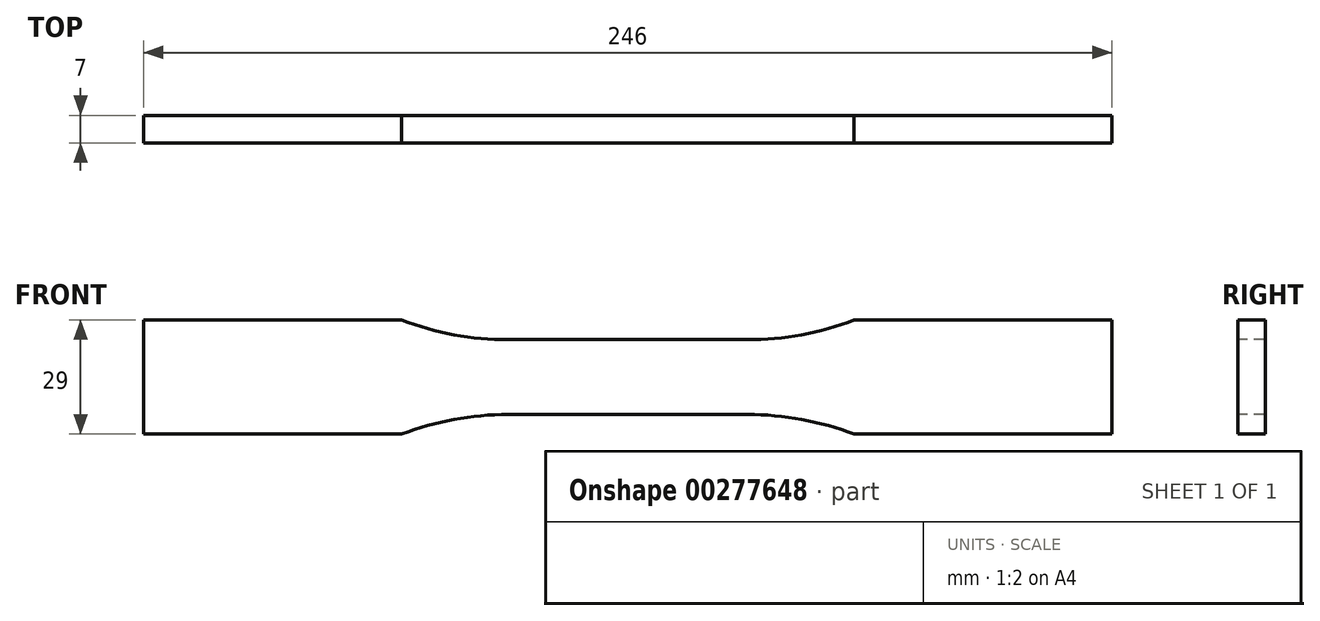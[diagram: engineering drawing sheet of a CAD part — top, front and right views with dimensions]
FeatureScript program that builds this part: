
annotation { "Feature Type Name" : "Feature", "Feature Type Description" : "" }
export const myFeature = defineFeature(function(context is Context, id is Id, definition is map)
    precondition{}
    {
        {
            var Q0;
            Q0=qCreatedBy(makeId("Front.planeOp"),FACE);
            var sketch = newSketch(context, id + "F0", { "sketchPlane" : qUnion([Q0])});
            skLineSegment(sketch, "E0", {"start": v(0, 9.5) * mm, "end": v(30.39, 9.5) * mm});
            skArc(sketch, "E1", {"start": v(30.39, 9.5) * mm, "mid": v(44.17, 10.76) * mm, "end": v(57.5, 14.5) * mm});
            skLineSegment(sketch, "E2", {"start": v(57.5, 14.5) * mm, "end": v(123, 14.5) * mm});
            skLineSegment(sketch, "E3.MirrorCS", {"start": v(57.5, -14.5) * mm, "end": v(123, -14.5) * mm});
            skLineSegment(sketch, "E4.MirrorCS", {"start": v(0, -9.5) * mm, "end": v(30.39, -9.5) * mm});
            skArc(sketch, "E5.MirrorCS", {"start": v(30.39, -9.5) * mm, "mid": v(44.17, -10.76) * mm, "end": v(57.5, -14.5) * mm});
            skArc(sketch, "E6.MirrorCS", {"start": v(-30.39, -9.5) * mm, "mid": v(-44.17, -10.76) * mm, "end": v(-57.5, -14.5) * mm});
            skLineSegment(sketch, "E7.MirrorCS", {"start": v(0, 9.5) * mm, "end": v(-30.39, 9.5) * mm});
            skArc(sketch, "E8.MirrorCS", {"start": v(-30.39, 9.5) * mm, "mid": v(-44.17, 10.76) * mm, "end": v(-57.5, 14.5) * mm});
            skLineSegment(sketch, "E9.MirrorCS", {"start": v(-57.5, -14.5) * mm, "end": v(-123, -14.5) * mm});
            skLineSegment(sketch, "E10.MirrorCS", {"start": v(0, -9.5) * mm, "end": v(-30.39, -9.5) * mm});
            skLineSegment(sketch, "E11.MirrorCS", {"start": v(-57.5, 14.5) * mm, "end": v(-123, 14.5) * mm});
            skLineSegment(sketch, "E12", {"start": v(-123, 14.5) * mm, "end": v(-123, -14.5) * mm});
            skLineSegment(sketch, "E13", {"start": v(123, 14.5) * mm, "end": v(123, -14.5) * mm});
            skSolve(sketch);
        }
        {
            var Q0;
            Q0 = qSketchRegion(id + "F0", true);
            extrude(context, id + "F1", {"entities" : qUnion([Q0]), "endBound" : BoundingType.SYMMETRIC, "oppositeDirection" : true, "depth" : 7 * mm});
        }
    });
